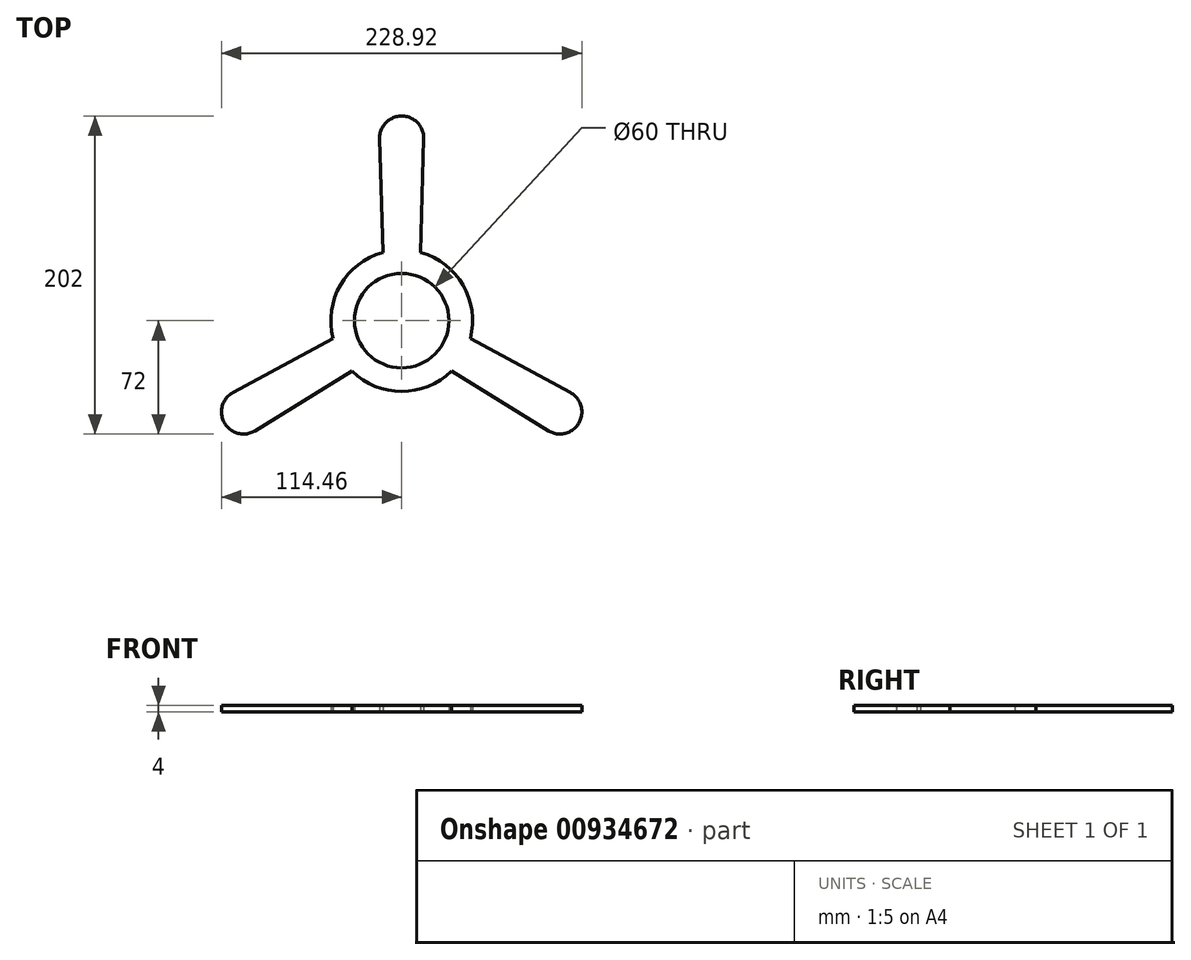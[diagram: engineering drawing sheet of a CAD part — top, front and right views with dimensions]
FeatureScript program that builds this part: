
annotation { "Feature Type Name" : "Feature", "Feature Type Description" : "" }
export const myFeature = defineFeature(function(context is Context, id is Id, definition is map)
    precondition{}
    {
        {
            var Q0;
            Q0=qCreatedBy(makeId("Top.planeOp"),FACE);
            var sketch = newSketch(context, id + "F0", { "sketchPlane" : qUnion([Q0])});
            skCircle(sketch, "E0", {"center": v(0, 0) * mm, "radius": 30 * mm});
            skArc(sketch, "E1", {"start": v(43.56, -11.3) * mm, "mid": v(38.97, 22.5) * mm, "end": v(12, 43.37) * mm});
            skLineSegment(sketch, "E2", {"start": v(0, 0) * mm, "end": v(0, 45) * mm, "construction": true});
            skLineSegment(sketch, "E3", {"start": v(-14, 115.6) * mm, "end": v(-12, 43.37) * mm});
            skLineSegment(sketch, "E4", {"start": v(14, 115.6) * mm, "end": v(12, 43.37) * mm});
            skLineSegment(sketch, "E5", {"start": v(0, 116) * mm, "end": v(0, 45) * mm, "construction": true});
            skArc(sketch, "E6", {"start": v(14, 115.6) * mm, "mid": v(0, 130) * mm, "end": v(-14, 115.6) * mm});
            skLineSegment(sketch, "E7", {"start": v(0, 0) * mm, "end": v(45, 0) * mm, "construction": true});
            skArc(sketch, "E8.1.0", {"start": v(93.12, -69.93) * mm, "mid": v(112.58, -65) * mm, "end": v(107.12, -45.68) * mm});
            skLineSegment(sketch, "E8.1.1", {"start": v(93.12, -69.93) * mm, "end": v(31.56, -32.08) * mm});
            skLineSegment(sketch, "E8.1.2", {"start": v(100.45, -58) * mm, "end": v(38.97, -22.5) * mm, "construction": true});
            skLineSegment(sketch, "E8.1.3", {"start": v(107.12, -45.68) * mm, "end": v(43.56, -11.3) * mm});
            skArc(sketch, "E8.2.0", {"start": v(-107.12, -45.68) * mm, "mid": v(-112.58, -65) * mm, "end": v(-93.12, -69.93) * mm});
            skLineSegment(sketch, "E8.2.1", {"start": v(-107.12, -45.68) * mm, "end": v(-43.56, -11.3) * mm});
            skLineSegment(sketch, "E8.2.2", {"start": v(-100.45, -58) * mm, "end": v(-38.97, -22.5) * mm, "construction": true});
            skLineSegment(sketch, "E8.2.3", {"start": v(-93.12, -69.93) * mm, "end": v(-31.56, -32.08) * mm});
            skLineSegment(sketch, "E8.anchor1", {"start": v(0, 0) * mm, "end": v(-12, 43.37) * mm, "construction": true});
            skLineSegment(sketch, "E8.anchor2", {"start": v(0, 0) * mm, "end": v(-31.56, -32.08) * mm, "construction": true});
            skArc(sketch, "E9.trimOffspring", {"start": v(-31.56, -32.08) * mm, "mid": v(0, -45) * mm, "end": v(31.56, -32.08) * mm});
            skArc(sketch, "E10.trimOffspring", {"start": v(-12, 43.37) * mm, "mid": v(-38.97, 22.5) * mm, "end": v(-43.56, -11.3) * mm});
            skSolve(sketch);
        }
        {
            var Q0;
            Q0=qSketchRegion(id+"F0",true);
            extrude(context, id + "F1", {"entities" : qUnion([Q0]), "depth" : 4 * mm, "offsetDistance" : 25 * mm});
        }
    });
